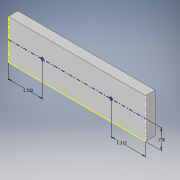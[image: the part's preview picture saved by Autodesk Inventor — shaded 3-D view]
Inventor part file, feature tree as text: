
AUTODESK INVENTOR PART (.ipt)
format: ipt  version: 2017 (Build 210142000, 142)  size: 103,424 bytes
history: native  units: in
note: dims shown in document units (in); Inventor stores cm internally (conversion verified against a paired STEP export)
features: sketch x2, extrude x1, hole x1
ambient origin geometry x8: Origin, YZ Plane, XZ Plane, XY Plane, X Axis, Y Axis, Z Axis, Center Point
bodies: Solid1 (feature_tree)
feature tree (4):
  extrude  "Extrusion1"  Depth=1.54in
  hole  "Hole1"  [1 undecoded]
  sketch  "Sketch1"  dims[d0=5.326in d1=1.54in]
  sketch  "Sketch2"  dims[d2=0.375in d3=0.0in d4=1.332in d5=1.332in d6=0.128in d7=0.315in d8=0.375in d9=0.25in d10=0.5635in d11=0.465in d12=0.8108in d13=0.77in]
note: 1 required parameter value undecoded (feature->parameter linkage not recoverable at this tier; creation-order binding heuristic only, values carry confidence <= 0.55)
